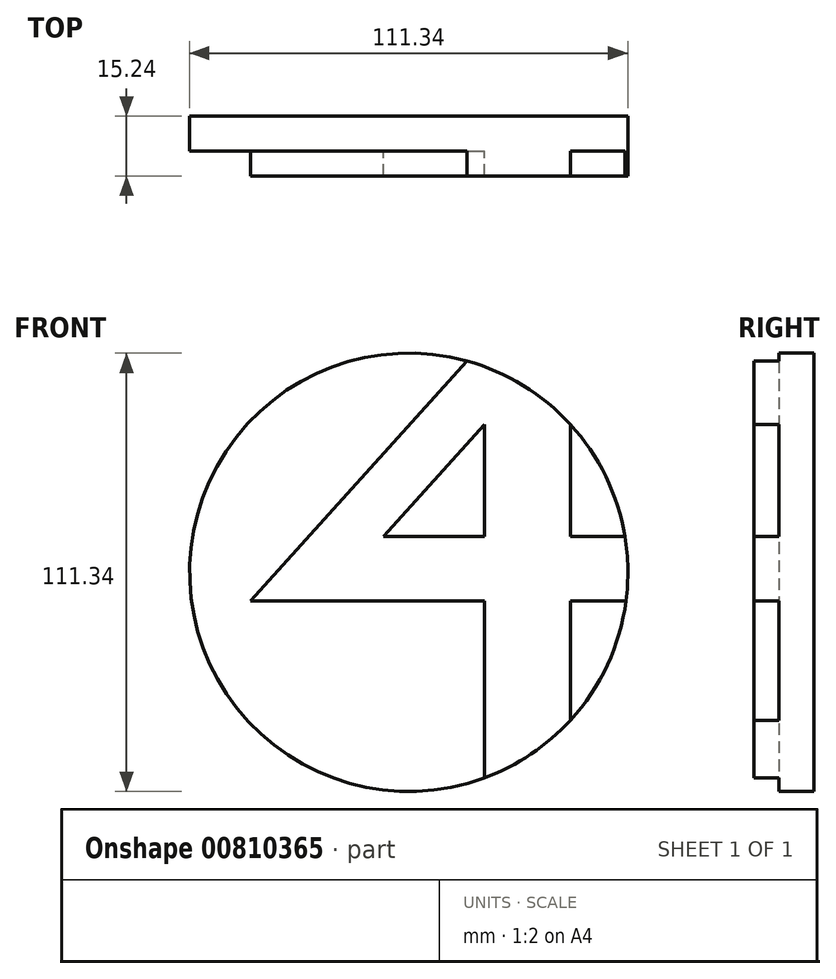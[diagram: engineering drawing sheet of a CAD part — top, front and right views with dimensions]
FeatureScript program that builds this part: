
annotation { "Feature Type Name" : "Feature", "Feature Type Description" : "" }
export const myFeature = defineFeature(function(context is Context, id is Id, definition is map)
    precondition{}
    {
        {
            var Q0;
            Q0=qCreatedBy(makeId("Front.planeOp"),FACE);
            var sketch = newSketch(context, id + "F0", { "sketchPlane" : qUnion([Q0])});
            skCircle(sketch, "E0", {"center": v(0, 0) * mm, "radius": 55.67 * mm});
            skSolve(sketch);
        }
        {
            var Q0;
            Q0 = qSketchRegion(id + "F0", true);
            extrude(context, id + "F1", {"entities" : qUnion([Q0]), "depth" : 8.9 * mm, "offsetDistance" : 25.4 * mm});
        }
        {
            var Q0;
            Q0=makeQuery(id+"F1.opExtrude","CAP_FACE",FACE,{"disambiguationData":[OSD([sQuery(id+"F0.wireOp",EDGE,"E0")])],"isStart":false});
            var sketch = newSketch(context, id + "F2", { "sketchPlane" : qUnion([Q0])});
            skLineSegment(sketch, "E1", {"start": v(41.08, -37.57) * mm, "end": v(41.08, -7.29) * mm});
            skLineSegment(sketch, "E2", {"start": v(41.08, -7.29) * mm, "end": v(55.2, -7.29) * mm});
            skLineSegment(sketch, "E3", {"start": v(-40.23, -7.29) * mm, "end": v(19.28, -7.29) * mm});
            skLineSegment(sketch, "E4", {"start": v(19.28, -7.29) * mm, "end": v(19.28, -52.23) * mm});
            skLineSegment(sketch, "E5", {"start": v(-40.23, -7.29) * mm, "end": v(14.8, 53.67) * mm});
            skLineSegment(sketch, "E6", {"start": v(41.08, 37.57) * mm, "end": v(41.08, 9.1) * mm});
            skLineSegment(sketch, "E7", {"start": v(41.08, 9.1) * mm, "end": v(54.92, 9.1) * mm});
            skLineSegment(sketch, "E8", {"start": v(19.28, 9.1) * mm, "end": v(19.28, 37.57) * mm});
            skLineSegment(sketch, "E9", {"start": v(19.28, 37.57) * mm, "end": v(-6.42, 9.1) * mm});
            skLineSegment(sketch, "E10", {"start": v(-6.42, 9.1) * mm, "end": v(19.28, 9.1) * mm});
            skSolve(sketch);
        }
        {
            var Q0;
            {var subQ3=sQuery(id+"F2.wireOp",EDGE,"E1");Q0=makeQuery(id+"F2.imprint","IMPRINT",FACE,{"disambiguationData":[TD([[makeQuery(id+"F2.imprint","IMPRINT",EDGE,{"derivedFrom":subQ3}),1.0]])]});}
            extrude(context, id + "F3", {"entities" : qUnion([Q0]), "operationType" : NewBodyOperationType.ADD, "depth" : 6.35 * mm, "offsetDistance" : 25.4 * mm});
        }
    });
